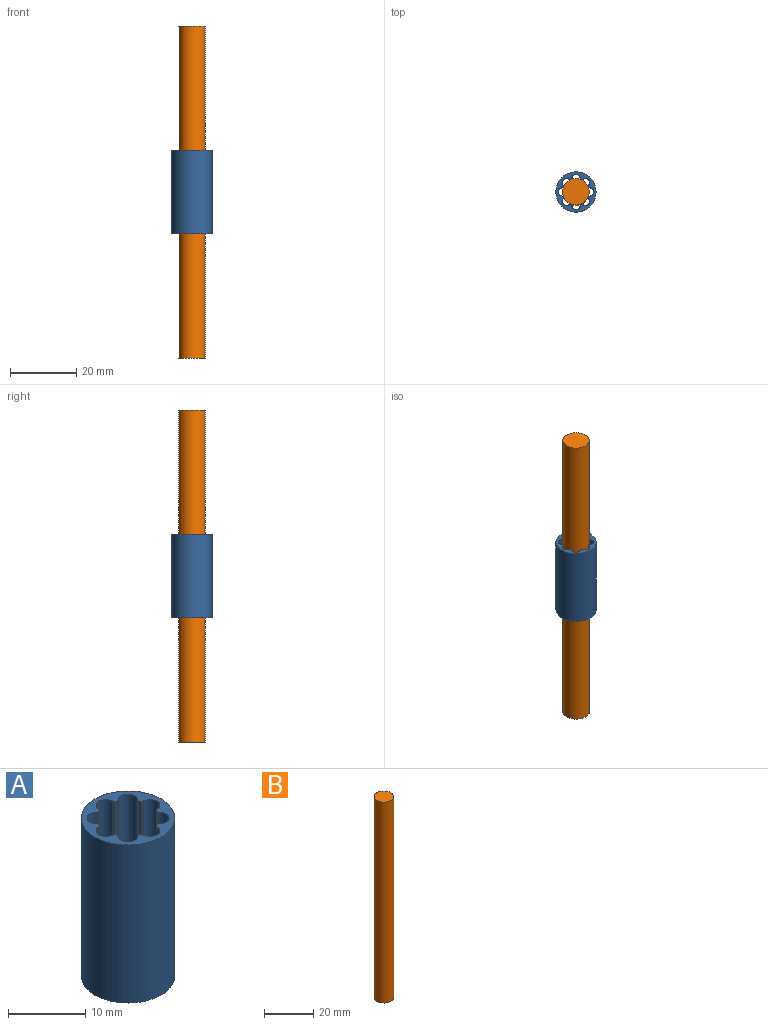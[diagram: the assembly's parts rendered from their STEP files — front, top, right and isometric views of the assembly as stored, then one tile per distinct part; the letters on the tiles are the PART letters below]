
ASSEMBLY  parts=2 mates=1
PART A: 35 faces, bbox 12.1x12.1x25 mm
  f0: cylinder r=4.05mm len=25mm, axis (0,0,-1), area 9.1mm2, adj f17,f18,f19,f34
  f1: cylinder r=1.25mm len=25mm, axis (0,0,-1), area 100.5mm2, adj f17,f18,f19,f20
  f2: cylinder r=4.05mm len=25mm, axis (0,0,-1), area 9.1mm2, adj f17,f18,f20,f21
  f3: cylinder r=1.25mm len=25mm, axis (0,0,-1), area 100.5mm2, adj f17,f18,f21,f22
  f4: cylinder r=4.05mm len=25mm, axis (0,0,-1), area 9.1mm2, adj f17,f18,f22,f23
  f5: cylinder r=1.25mm len=25mm, axis (0,0,-1), area 100.5mm2, adj f17,f18,f23,f24
  f6: cylinder r=4.05mm len=25mm, axis (0,0,-1), area 9.1mm2, adj f17,f18,f24,f25
  f7: cylinder r=1.25mm len=25mm, axis (0,0,-1), area 100.5mm2, adj f17,f18,f25,f26
  f8: cylinder r=4.05mm len=25mm, axis (0,0,-1), area 9.1mm2, adj f17,f18,f26,f27
  f9: cylinder r=1.25mm len=25mm, axis (0,0,-1), area 100.5mm2, adj f17,f18,f27,f28
  f10: cylinder r=4.05mm len=25mm, axis (0,0,-1), area 9.1mm2, adj f17,f18,f28,f29
  f11: cylinder r=1.25mm len=25mm, axis (0,0,-1), area 100.5mm2, adj f17,f18,f29,f30
  f12: cylinder r=4.05mm len=25mm, axis (0,0,-1), area 9.1mm2, adj f17,f18,f30,f31
  f13: cylinder r=1.25mm len=25mm, axis (0,0,-1), area 100.5mm2, adj f17,f18,f31,f32
  f14: cylinder r=4.05mm len=25mm, axis (0,0,-1), area 9.1mm2, adj f17,f18,f32,f33
  f15: cylinder r=1.25mm len=25mm, axis (0,0,-1), area 100.5mm2, adj f17,f18,f33,f34
  f16: cylinder r=6.05mm len=25mm, axis (0,0,-1), area 950.3mm2, adj f17,f18
  f17: plane 12.1x12.1mm, normal (0,0,1), area 42.5mm2, adj f0,f1,f2,f3,f4,f5,f6,f7
  f18: plane 12.1x12.1mm, normal (0,0,-1), area 42.5mm2, adj f0,f1,f2,f3,f4,f5,f6,f7
  f19: cylinder r=0.2mm len=25mm, axis (0,0,-1), area 6.3mm2, adj f0,f1,f17,f18
  f20: cylinder r=0.2mm len=25mm, axis (0,0,-1), area 6.3mm2, adj f1,f2,f17,f18
  f21: cylinder r=0.2mm len=25mm, axis (0,0,-1), area 6.3mm2, adj f2,f3,f17,f18
  f22: cylinder r=0.2mm len=25mm, axis (0,0,-1), area 6.3mm2, adj f3,f4,f17,f18
  f23: cylinder r=0.2mm len=25mm, axis (0,0,-1), area 6.3mm2, adj f4,f5,f17,f18
  f24: cylinder r=0.2mm len=25mm, axis (0,0,-1), area 6.3mm2, adj f5,f6,f17,f18
  f25: cylinder r=0.2mm len=25mm, axis (0,0,-1), area 6.3mm2, adj f6,f7,f17,f18
  f26: cylinder r=0.2mm len=25mm, axis (0,0,-1), area 6.3mm2, adj f7,f8,f17,f18
  f27: cylinder r=0.2mm len=25mm, axis (0,0,-1), area 6.3mm2, adj f8,f9,f17,f18
  f28: cylinder r=0.2mm len=25mm, axis (0,0,-1), area 6.3mm2, adj f9,f10,f17,f18
  f29: cylinder r=0.2mm len=25mm, axis (0,0,-1), area 6.3mm2, adj f10,f11,f17,f18
  f30: cylinder r=0.2mm len=25mm, axis (0,0,-1), area 6.3mm2, adj f11,f12,f17,f18
  f31: cylinder r=0.2mm len=25mm, axis (0,0,-1), area 6.3mm2, adj f12,f13,f17,f18
  f32: cylinder r=0.2mm len=25mm, axis (0,0,-1), area 6.3mm2, adj f13,f14,f17,f18
  f33: cylinder r=0.2mm len=25mm, axis (0,0,-1), area 6.3mm2, adj f14,f15,f17,f18
  f34: cylinder r=0.2mm len=25mm, axis (0,0,-1), area 6.3mm2, adj f0,f15,f17,f18
PART B: 3 faces, bbox 8x8x100 mm
  f0: cylinder r=4mm len=100mm, axis (0,0,-1), area 2513.3mm2, adj f1,f2
  f1: plane 8x8mm, normal (0,0,1), area 50.3mm2, adj f0
  f2: plane 8x8mm, normal (0,0,-1), area 50.3mm2, adj f0
PLACE A t=(-21.49,0.41,6.73)mm
PLACE B t=(-53.62,0.41,-30.77)mm
MATE slider A.f0 <-> B.f0  axis (0,0,-1) through (-21.49,0.41,19.23)mm
